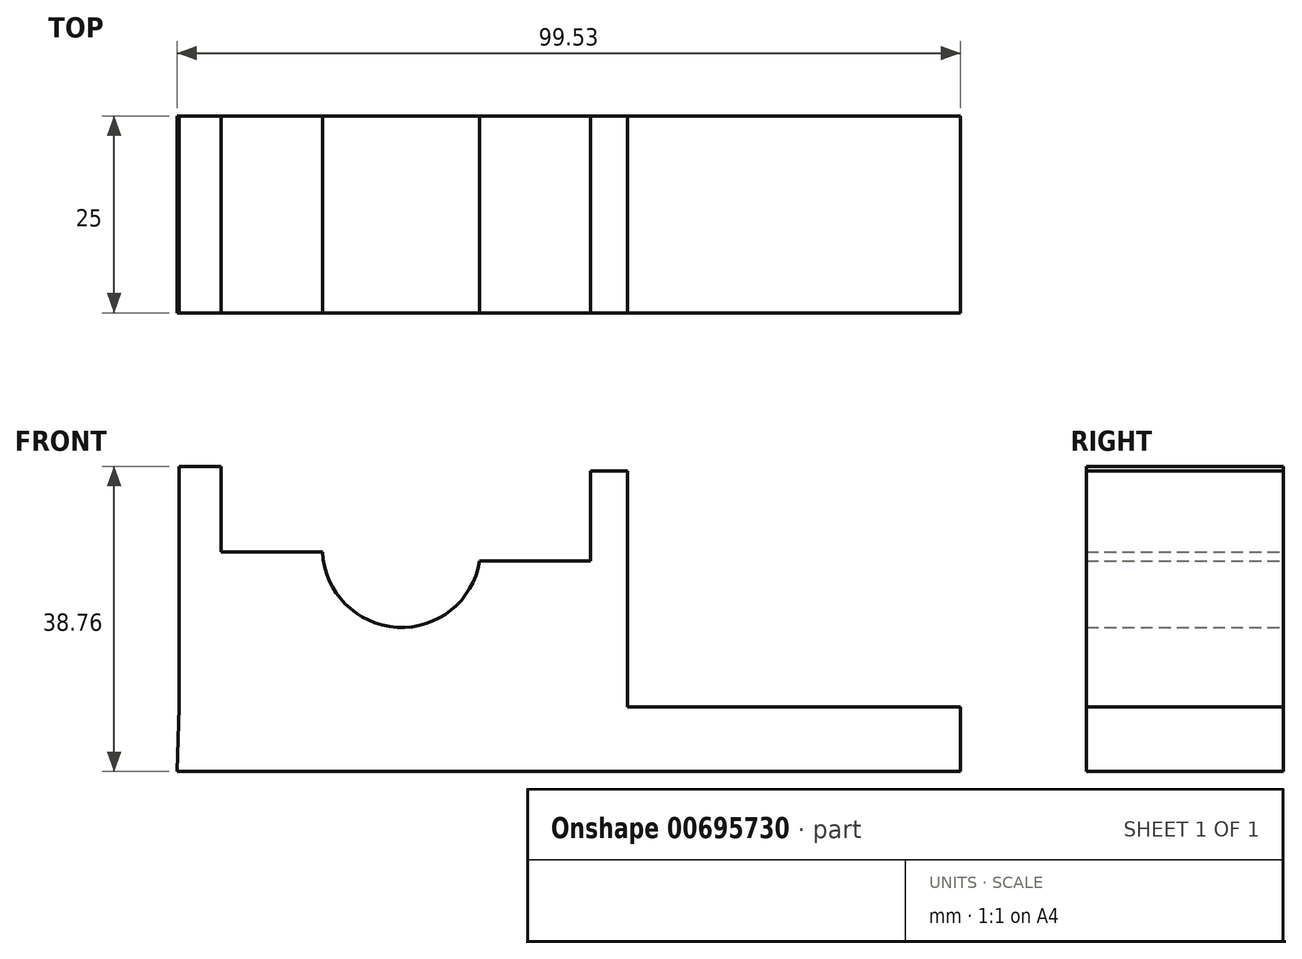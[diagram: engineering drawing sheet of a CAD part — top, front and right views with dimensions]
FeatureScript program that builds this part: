
annotation { "Feature Type Name" : "Feature", "Feature Type Description" : "" }
export const myFeature = defineFeature(function(context is Context, id is Id, definition is map)
    precondition{}
    {
        {
            var Q0;
            Q0=qCreatedBy(makeId("Front.planeOp"),FACE);
            var sketch = newSketch(context, id + "F0", { "sketchPlane" : qUnion([Q0])});
            skLineSegment(sketch, "E0", {"start": v(-63.57, 56.67) * mm, "end": v(-58.28, 56.67) * mm});
            skLineSegment(sketch, "E1", {"start": v(-58.28, 56.67) * mm, "end": v(-58.28, 45.8) * mm});
            skLineSegment(sketch, "E2", {"start": v(-58.28, 45.8) * mm, "end": v(-45.36, 45.8) * mm});
            skLineSegment(sketch, "E3", {"start": v(-63.57, 56.67) * mm, "end": v(-63.57, 38.46) * mm});
            skLineSegment(sketch, "E4", {"start": v(-6.6, 37.58) * mm, "end": v(-6.6, 56.08) * mm});
            skLineSegment(sketch, "E5", {"start": v(-6.6, 56.08) * mm, "end": v(-11.3, 56.08) * mm});
            skLineSegment(sketch, "E6", {"start": v(-11.3, 56.08) * mm, "end": v(-11.3, 44.63) * mm});
            skLineSegment(sketch, "E7", {"start": v(-11.3, 44.63) * mm, "end": v(-25.4, 44.63) * mm});
            skLineSegment(sketch, "E8", {"start": v(-63.57, 26.13) * mm, "end": v(35.67, 26.13) * mm});
            skLineSegment(sketch, "E9", {"start": v(35.67, 26.13) * mm, "end": v(35.67, 17.91) * mm});
            skLineSegment(sketch, "E10", {"start": v(35.67, 17.91) * mm, "end": v(-63.86, 17.91) * mm});
            skLineSegment(sketch, "E11", {"start": v(-63.86, 17.91) * mm, "end": v(-63.57, 26.13) * mm});
            skLineSegment(sketch, "E12", {"start": v(-63.57, 38.46) * mm, "end": v(-63.57, 26.13) * mm});
            skLineSegment(sketch, "E13", {"start": v(-6.6, 37.58) * mm, "end": v(-6.6, 26.13) * mm});
            skArc(sketch, "E14", {"start": v(-45.36, 45.8) * mm, "mid": v(-35.9, 36.23) * mm, "end": v(-25.4, 44.63) * mm});
            skSolve(sketch);
        }
        {
            var Q0;
            Q0 = qSketchRegion(id + "F0", true);
            extrude(context, id + "F1", {"entities" : qUnion([Q0]), "depth" : 25 * mm, "offsetDistance" : 25 * mm});
        }
    });
